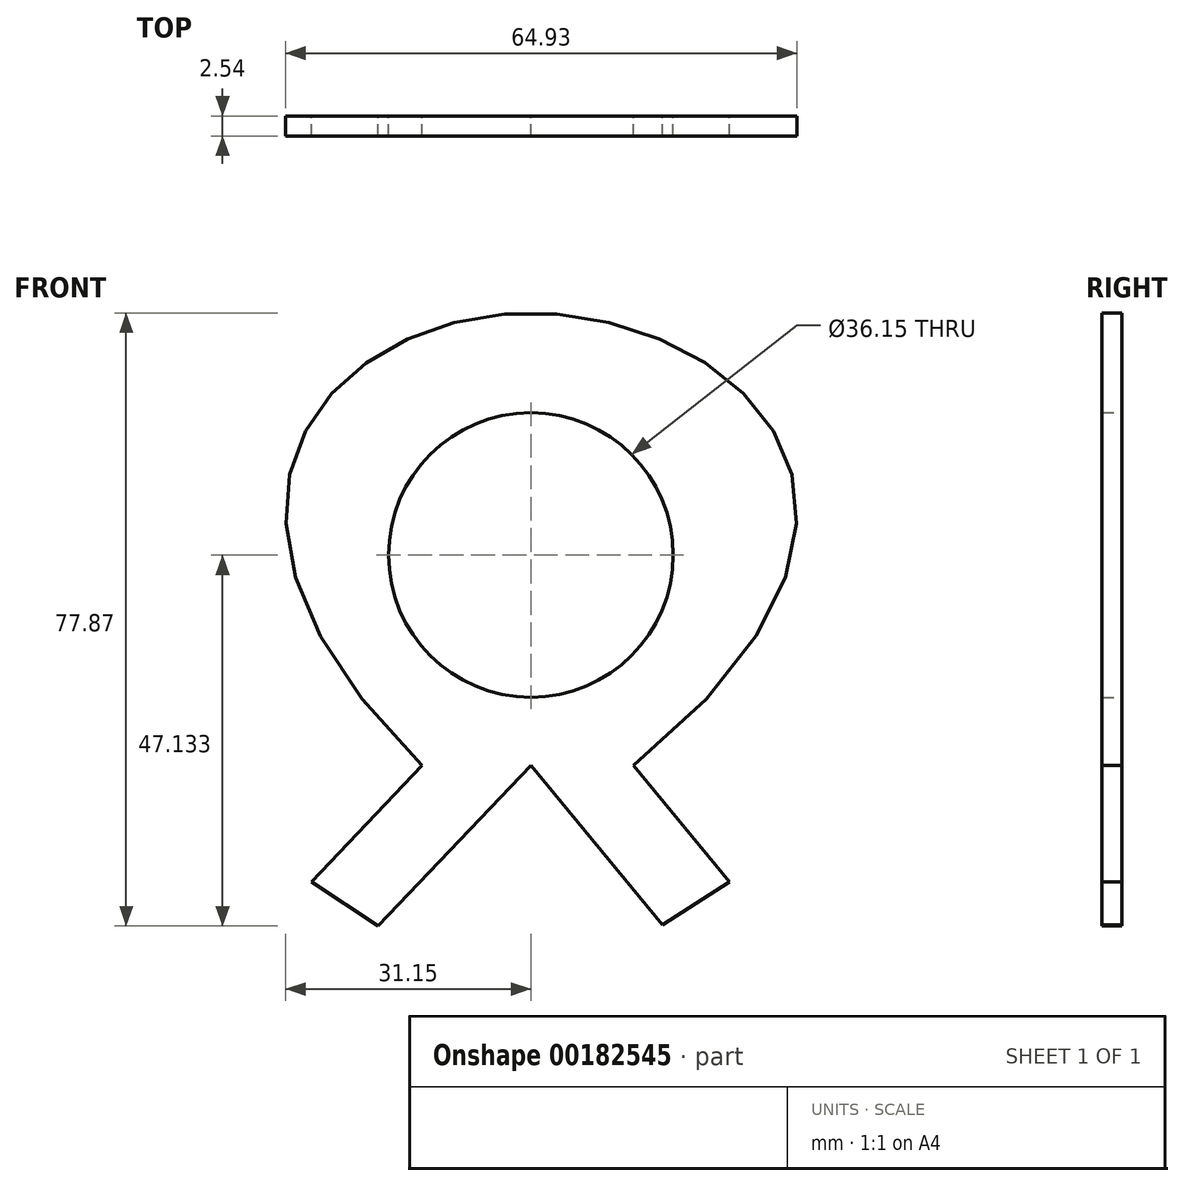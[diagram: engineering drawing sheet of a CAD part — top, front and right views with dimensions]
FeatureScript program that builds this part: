
annotation { "Feature Type Name" : "Feature", "Feature Type Description" : "" }
export const myFeature = defineFeature(function(context is Context, id is Id, definition is map)
    precondition{}
    {
        {
            var Q0;
            Q0=qCreatedBy(makeId("Front.planeOp"),FACE);
            var sketch = newSketch(context, id + "F0", { "sketchPlane" : qUnion([Q0])});
            skLineSegment(sketch, "E0", {"start": v(0, 0) * mm, "end": v(16.7, -20.26) * mm});
            skLineSegment(sketch, "E1", {"start": v(0, 0) * mm, "end": v(-19.43, -20.38) * mm});
            skLineSegment(sketch, "E2", {"start": v(13.05, 0) * mm, "end": v(25.24, -14.75) * mm});
            skLineSegment(sketch, "E3", {"start": v(25.24, -14.75) * mm, "end": v(16.7, -20.26) * mm});
            skLineSegment(sketch, "E4", {"start": v(-13.83, 0) * mm, "end": v(-27.9, -14.75) * mm});
            skLineSegment(sketch, "E5", {"start": v(-27.9, -14.75) * mm, "end": v(-19.43, -20.38) * mm});
            skFitSpline(sketch, "E6", {"points": [v(-13.83, 0) * mm, v(0, 57.5) * mm, v(13.05, 0) * mm], "startDerivative": vector(-203.98, 199.07) * mm, "endDerivative": vector(-247.5, -199.37) * mm});
            skCircle(sketch, "E7", {"center": v(0, 26.75) * mm, "radius": 18.07 * mm});
            skSolve(sketch);
        }
        {
            var Q0;
            Q0=makeQuery(id+"F0.imprint","IMPRINT",FACE,{"disambiguationData":[TD([[makeQuery(id+"F0.imprint","IMPRINT",EDGE,{"derivedFrom":sQuery(id+"F0.wireOp",EDGE,"E0")}),1.0]])]});
            extrude(context, id + "F1", {"entities" : qUnion([Q0]), "depth" : 2.54 * mm});
        }
    });
